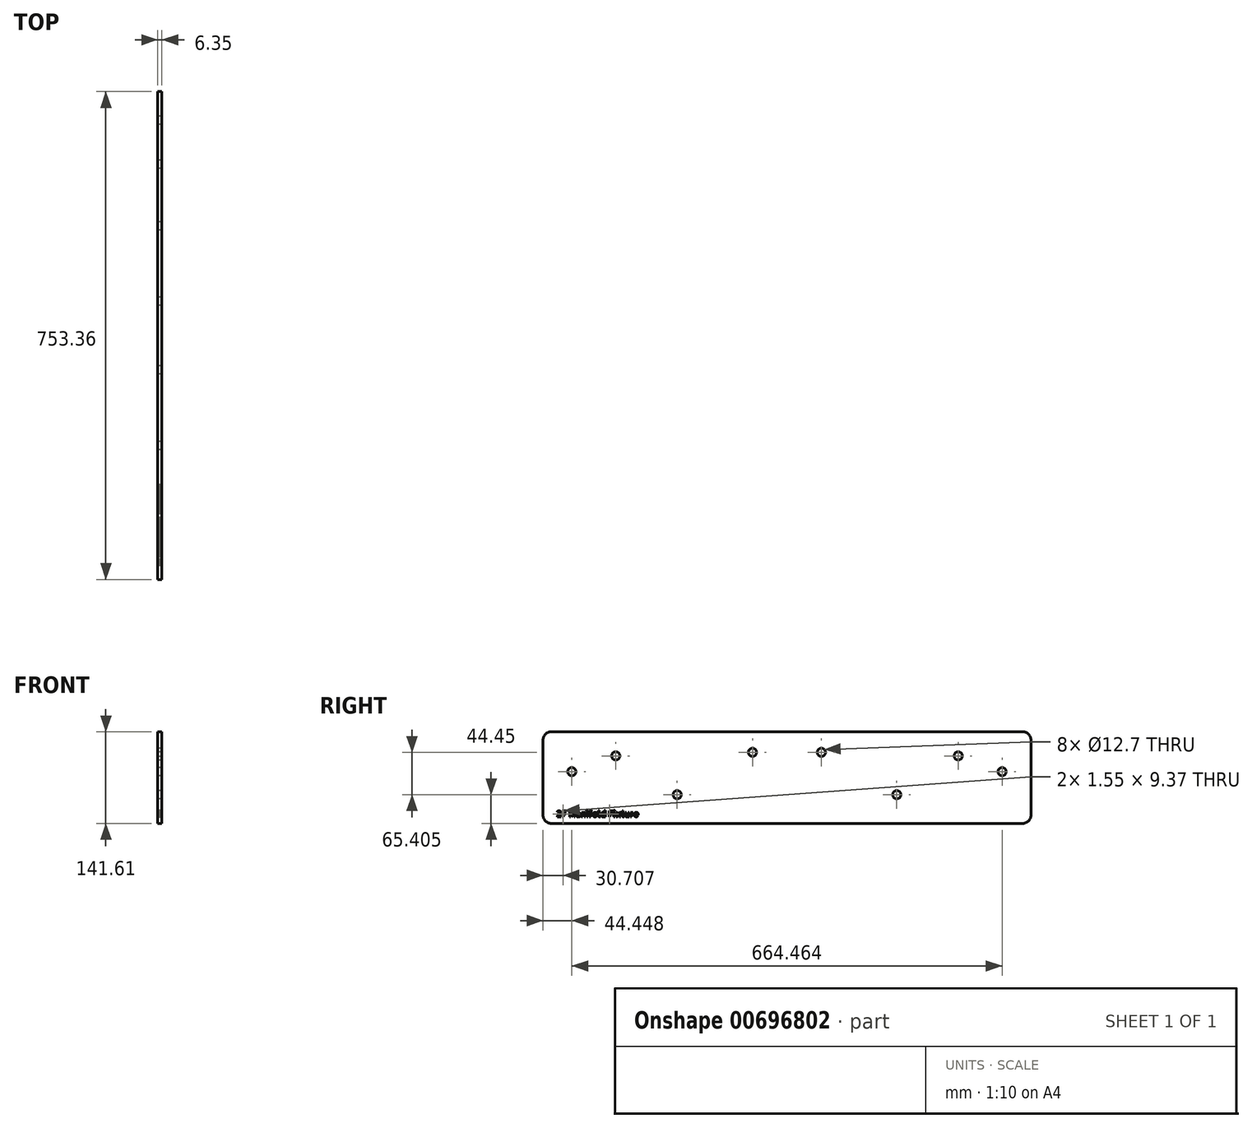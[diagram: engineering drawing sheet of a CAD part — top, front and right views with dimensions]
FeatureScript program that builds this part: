
annotation { "Feature Type Name" : "Feature", "Feature Type Description" : "" }
export const myFeature = defineFeature(function(context is Context, id is Id, definition is map)
    precondition{}
    {
        {
            var Q0;
            Q0=qCreatedBy(makeId("Right.planeOp"),FACE);
            var sketch = newSketch(context, id + "F0", { "sketchPlane" : qUnion([Q0])});
            skLineSegment(sketch, "E0", {"start": v(-332.23, 0) * mm, "end": v(332.23, 0) * mm, "construction": true});
            skCircle(sketch, "E1", {"center": v(-332.23, 0) * mm, "radius": 6.35 * mm});
            skCircle(sketch, "E2", {"center": v(332.23, 0) * mm, "radius": 6.35 * mm});
            skPoint(sketch, "E3", {"position": v(0, 0) * mm});
            skCircle(sketch, "E4", {"center": v(-53.18, 29.85) * mm, "radius": 6.35 * mm});
            skCircle(sketch, "E5", {"center": v(53.18, 29.85) * mm, "radius": 6.35 * mm});
            skLineSegment(sketch, "E6", {"start": v(-53.18, 29.85) * mm, "end": v(53.18, 29.85) * mm, "construction": true});
            skLineSegment(sketch, "E7", {"start": v(0, -114.6) * mm, "end": v(0, 144.87) * mm, "construction": true});
            skPoint(sketch, "E8", {"position": v(0, 29.85) * mm});
            skCircle(sketch, "E9", {"center": v(264.41, 24.38) * mm, "radius": 6.35 * mm});
            skCircle(sketch, "E10", {"center": v(-264.41, 24.38) * mm, "radius": 6.35 * mm});
            skLineSegment(sketch, "E11", {"start": v(-264.41, 24.38) * mm, "end": v(264.41, 24.38) * mm, "construction": true});
            skPoint(sketch, "E12", {"position": v(0, 24.38) * mm});
            skCircle(sketch, "E13", {"center": v(-169.54, -35.56) * mm, "radius": 6.35 * mm});
            skCircle(sketch, "E14", {"center": v(169.54, -35.56) * mm, "radius": 6.35 * mm});
            skLineSegment(sketch, "E15", {"start": v(-169.54, -35.56) * mm, "end": v(169.54, -35.56) * mm, "construction": true});
            skPoint(sketch, "E16", {"position": v(0, 45.96) * mm});
            skPoint(sketch, "E17", {"position": v(0, -35.56) * mm});
            skLineSegment(sketch, "E18.bottom", {"start": v(-376.68, 61.6) * mm, "end": v(376.68, 61.6) * mm});
            skLineSegment(sketch, "E18.top", {"start": v(-376.68, -80.01) * mm, "end": v(376.68, -80.01) * mm});
            skLineSegment(sketch, "E18.left", {"start": v(-376.68, 61.6) * mm, "end": v(-376.68, -80.01) * mm});
            skLineSegment(sketch, "E18.right", {"start": v(376.68, 61.6) * mm, "end": v(376.68, -80.01) * mm});
            skSolve(sketch);
        }
        {
            var Q0;
            Q0 = qSketchRegion(id + "F0", true);
            extrude(context, id + "F1", {"entities" : qUnion([Q0]), "depth" : 6.35 * mm, "offsetDistance" : 25.4 * mm});
        }
        {
            var Q0;
            Q0=makeQuery(id+"F1.opExtrude","SWEPT_EDGE",EDGE,{"disambiguationData":[OSD([sQuery(id+"F0.wireOp",EDGE,"E18.bottom"),sQuery(id+"F0.wireOp",EDGE,"E18.left")])]});
            var Q1;
            Q1=makeQuery(id+"F1.opExtrude","SWEPT_EDGE",EDGE,{"disambiguationData":[OSD([sQuery(id+"F0.wireOp",EDGE,"E18.top"),sQuery(id+"F0.wireOp",EDGE,"E18.left")])]});
            var Q2;
            Q2=makeQuery(id+"F1.opExtrude","SWEPT_EDGE",EDGE,{"disambiguationData":[OSD([sQuery(id+"F0.wireOp",EDGE,"E18.bottom"),sQuery(id+"F0.wireOp",EDGE,"E18.right")])]});
            var Q3;
            Q3=makeQuery(id+"F1.opExtrude","SWEPT_EDGE",EDGE,{"disambiguationData":[OSD([sQuery(id+"F0.wireOp",EDGE,"E18.top"),sQuery(id+"F0.wireOp",EDGE,"E18.right")])]});
            fillet(context, id + "F2", {"entities" : qUnion([Q0, Q1, Q2, Q3]), "radius" : 12.7 * mm, "tangentPropagation" : true, "allowEdgeOverflow" : false});
        }
        {
            var Q0;
            Q0=makeQuery(id+"F1.opExtrude","CAP_FACE",FACE,{"disambiguationData":[OSD([sQuery(id+"F0.wireOp",EDGE,"E1"),sQuery(id+"F0.wireOp",EDGE,"E2"),sQuery(id+"F0.wireOp",EDGE,"E4"),sQuery(id+"F0.wireOp",EDGE,"E5"),sQuery(id+"F0.wireOp",EDGE,"E9"),sQuery(id+"F0.wireOp",EDGE,"E10"),sQuery(id+"F0.wireOp",EDGE,"E13"),sQuery(id+"F0.wireOp",EDGE,"E14"),sQuery(id+"F0.wireOp",EDGE,"E18.bottom"),sQuery(id+"F0.wireOp",EDGE,"E18.top"),sQuery(id+"F0.wireOp",EDGE,"E18.left"),sQuery(id+"F0.wireOp",EDGE,"E18.right")])],"isStart":false});
            var sketch = newSketch(context, id + "F3", { "sketchPlane" : qUnion([Q0])});
            skText(sketch, "E19", { "text": "2F Manifold Fixture", "fontName": "AllertaStencil-Regular.ttf"});
            const initialGuessF3  = {"E19": [-0.35576, -0.06986, 1, 0, 0.00937]};
            skSetInitialGuess(sketch, initialGuessF3);
            skSolve(sketch);
        }
        {
            var Q0;
            Q0 = qSketchRegion(id + "F3", true);
            extrude(context, id + "F4", {"entities" : qUnion([Q0]), "operationType" : NewBodyOperationType.REMOVE, "endBound" : BoundingType.THROUGH_ALL, "oppositeDirection" : true, "depth" : 25.4 * mm, "offsetDistance" : 25.4 * mm});
        }
    });
